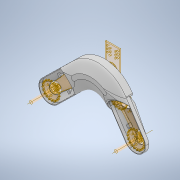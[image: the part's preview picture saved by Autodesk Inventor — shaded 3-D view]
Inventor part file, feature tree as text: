
AUTODESK INVENTOR PART (.ipt)
format: ipt  version: 2020.1 (Build 241239000, 239)  size: 5,488,128 bytes
history: native  units: mm
features: other x30, sketch x16, surface_op x12, extrude x9, plane x5, loft x3, shell x3, hole x2, chamfer x2, revolve x2, projected_geometry x2
ambient origin geometry x8: Origin, YZ Plane, XZ Plane, XY Plane, X Axis, Y Axis, Z Axis, Center Point
bodies: body (feature_tree)
feature tree (86):
  other  "Lenkerhuelle V2"
  plane  "Work Plane1"
  sketch  "Sketch1"  dims[d0=3.0mm d1=3.0mm]
  sketch  "Sketch2"  dims[d2=3.0mm d3=3.0mm]
  plane  "Work Plane2"
  sketch  "Sketch3"  dims[d4=3.0mm d5=5.0mm d6=75.0mm]
  sketch  "Sketch4"  dims[d8=75.0mm d9=75.0mm d10=0.0mm d11=90.0deg]
  loft  "Loft1"
  loft  "Loft2"
  extrude  "Extrusion3"  Depth=5.0mm
  shell  "Shell3"  Thickness=75.0mm
  extrude  "Extrusion4"  Depth=75.0mm
  shell  "Shell4"  Thickness=0.0mm
  sketch  "Sketch10"  dims[d27=11.0mm d28=0.0mm d29=35.0mm]
  hole  "Hole1"  [1 undecoded]
  hole  "Hole2"  [1 undecoded]
  sketch  "Sketch11"  dims[d30=35.0mm d31=2.0mm]
  extrude  "Extrusion5"  Depth=35.0mm
  extrude  "Extrusion6"  Depth=2.0mm
  extrude  "Extrusion7"  Depth=1.0mm
  chamfer  "Chamfer1"  Distance=23.7mm
  extrude  "Extrusion8"  Depth=0.2mm
  chamfer  "Chamfer2"  Distance=10.0mm
  sketch  "Sketch14"  dims[d47=1.0mm d48=23.7mm d49=0.0mm]
  plane  "Work Plane3"
  loft  "Loft3"
  plane  "Work Plane4"
  revolve  "Revolution1"  [1 undecoded]
  plane  "Work Plane5"
  revolve  "Revolution2"  [1 undecoded]
  shell  "Shell5"  Thickness=15.0mm
  extrude  "Extrusion9"  Depth=0.5mm
  sketch  "Sketch19"  dims[d64=2.0mm d65=2.0mm d66=45.0deg d67=95.0mm d68=15.0mm d69=15.0mm d74=7.0mm d75=90.0deg d76=0.0mm d77=90.0deg d78=90.0deg d79=95.0mm d80=90.0deg d81=90.0deg d82=24.43461mm d83=95.0mm d84=24.43461mm d85=90.0deg d86=2.0mm d87=1.0mm d88=1.0mm d89=1.0mm d90=1.0mm d91=11.0mm d92=0.0mm d93=8.2mm d94=8.2mm d95=12.0mm d96=12.0mm d97=10.0mm d98=0.349066mm d99=5.0mm d100=0.0mm d101=0.5mm d102=0.872665mm d103=0.5mm d104=0.872665mm]
  extrude  "Extrusion10"  Depth=0.5mm TaperAngle=90.0deg
  extrude  "Extrusion11"  TaperAngle=90.0deg  [1 undecoded]
  other  "Lenkerhuelle V1"
  sketch  "Sketch8"  dims[d12=0.0mm d13=90.0deg d14=0.0mm d15=90.0deg d16=0.0mm d17=90.0deg]
  projected_geometry  "Projected Loop3"
  sketch  "Sketch9"  dims[d24=11.0mm d25=0.0mm d26=2.0mm]
  projected_geometry  "Projected Loop4"
  sketch  "Sketch12"  dims[d32=5.0mm d33=6.0mm d34=4.0mm d35=2.0mm d36=90.0deg d37=8.0mm d38=20.594885mm]
  sketch  "Sketch13"  dims[d39=5.0mm d40=6.0mm d41=4.0mm d42=2.0mm d43=90.0deg d44=8.0mm d45=20.594885mm d46=1.0mm]
  sketch  "Sketch15"  dims[d50=23.7mm d51=0.0mm d52=0.2mm]
  other  "Lekerabdeckung VA"
  other  "Work Axis1"
  sketch  "Sketch16"  dims[d54=12.0mm d55=10.0mm d56=0.0mm]
  other  "Work Axis2"
  sketch  "Sketch17"  dims[d57=2.0mm d58=2.0mm d59=45.0deg d60=0.2mm]
  sketch  "Sketch18"  dims[d61=12.0mm d62=10.0mm d63=0.0mm]
  surface_op  "Surface1"
  surface_op  "Surface2"
  surface_op  "Surface3"
  surface_op  "Surface4"
  surface_op  "Surface5"
  surface_op  "Surface6"
  surface_op  "Surface7"
  surface_op  "Surface8"
  surface_op  "Surface9"
  surface_op  "Surface10"
  surface_op  "Surface11"
  surface_op  "Surface12"
  other  "Srf1"
  other  "Srf2"
  other  "Srf3"
  other  "Srf4"
  other  "Srf5"
  other  "Srf6"
  other  "Srf7"
  other  "Srf8"
  other  "Srf9"
  other  "Srf10"
  other  "Srf11"
  other  "Srf12"
  other  "<userpath>\Desktop\URBANT ROVER\rover.iam"
  other  "rover.iam"
  other  "swing R"
  other  "EXACT SWING.1"
  other  "Kettenradaufnahme.1"
  other  "swing axle connector.1"
  other  "Kettenradaufnahme.2"
  other  "Rad mit Aufnahme.5"
  other  "Axle Nut.2"
  other  "drive shaft.2"
  other  "Axle Nut.3"
  other  "drive shaft.1"
  other  "Rad mit Aufnahme.4"
note: 5 required parameter values undecoded (feature->parameter linkage not recoverable at this tier; creation-order binding heuristic only, values carry confidence <= 0.55)